SOLIDWORKS PART (.sldprt)
format: sldprt  version: not decoded by parser v0  size: 259,072 bytes
history: native  units: mm
features: sketch x7, cut_extrude x5, plane x3, extrude x2, material x1, chamfer x1, fillet x1 (+8 scaffold rows collapsed)
feature tree (28):
  scaffold x8  (default folders/planes/origin — collapsed)
  material  "Matériau <non spécifié>"
  plane  "Face"
  plane  "Dessus"
  plane  "Droite"
  sketch  "Esquisse1"  dims[D1=9.97mm D2=7.55mm]
  extrude  "Extrusion1"  Depth=10.02mm
  chamfer  "Chanfrein1"  Distance=3.55mm Angle=25deg
  sketch  "Esquisse2"  dims[D1=3.45mm]
  cut_extrude  "Enlèv. mat.-Extru.1"  Depth=1mm
  sketch  "Esquisse3"  dims[c1.D1=5.0mm c1.D2=4.0mm c1.D3=0.8mm c1.D4=0.67mm c2.D3=0.8mm c2.D4=0.9mm]
  cut_extrude  "Enlèv. mat.-Extru.2"  Depth=1.6mm
  sketch  "Esquisse4"  dims[D1=3.35mm]
  cut_extrude  "Enlèv. mat.-Extru.3"  Depth=1.6mm
  sketch  "Esquisse5"  dims[D1=1.0mm D2=5.2mm]
  extrude  "Extrusion2"  Depth=5mm
  fillet  "Congé1"  Radius=0.5mm
  sketch  "Esquisse7"
  cut_extrude  "Enlèv. mat.-Extru.4"  Depth=0.5mm
  sketch  "Esquisse8"
  cut_extrude  "Enlèv. mat.-Extru.5"  Depth=0.5mm
decode coverage: 14 of 16 modeling features carry decoded parameters
note: suppression state not decoded; provenance and decode notes live in map.json
